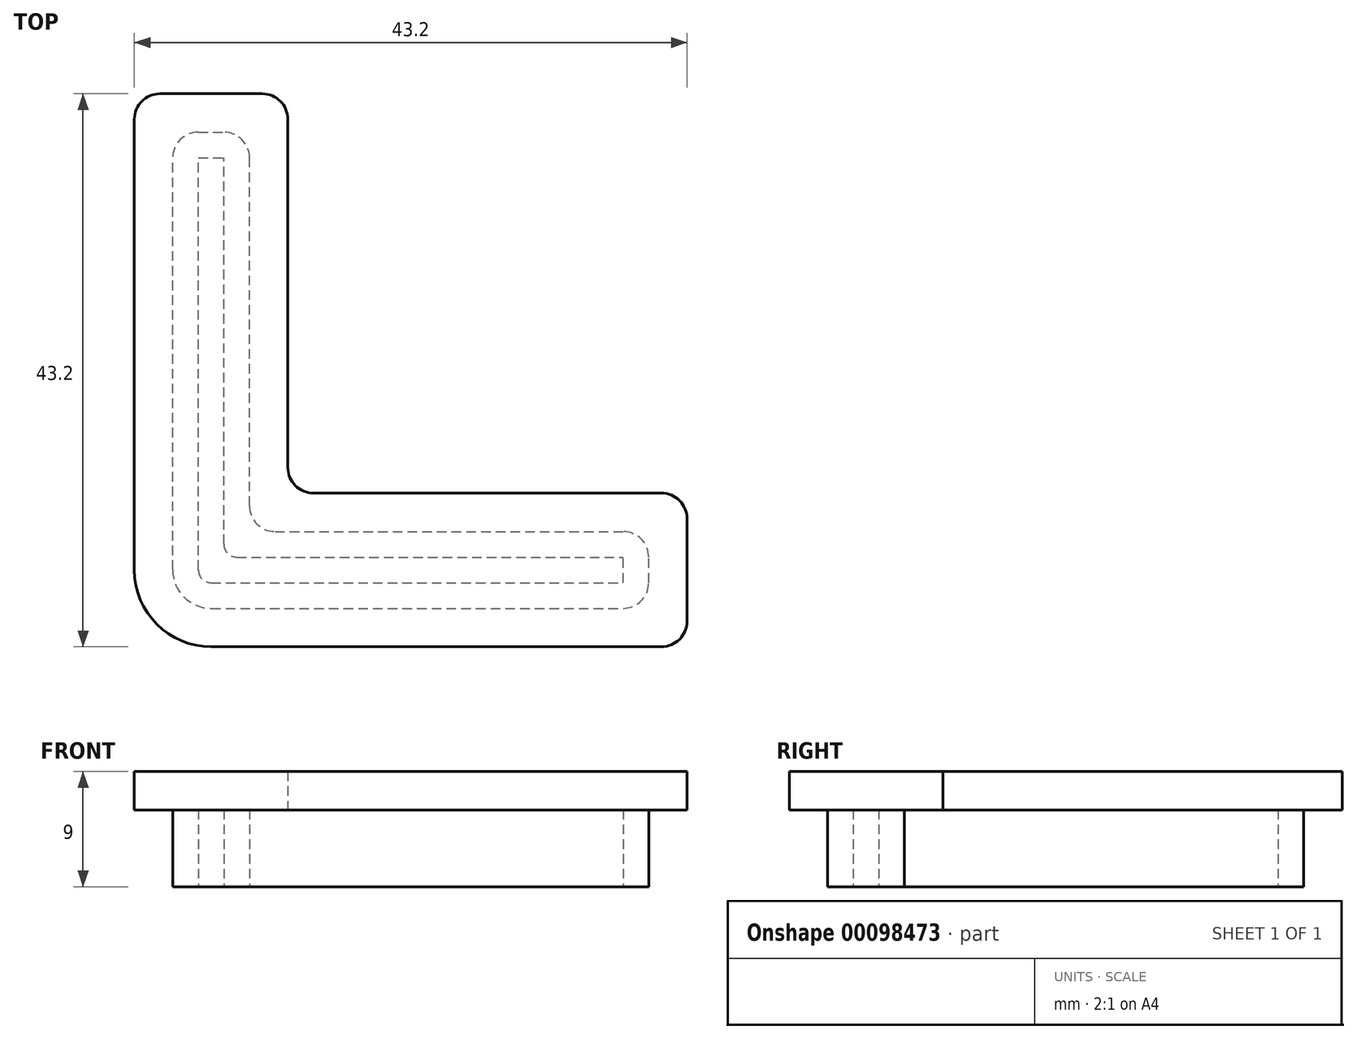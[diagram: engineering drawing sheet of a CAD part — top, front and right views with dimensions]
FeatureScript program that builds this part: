
annotation { "Feature Type Name" : "Feature", "Feature Type Description" : "" }
export const myFeature = defineFeature(function(context is Context, id is Id, definition is map)
    precondition{}
    {
        {
            var Q0;
            Q0=qCreatedBy(makeId("Top.planeOp"),FACE);
            var sketch = newSketch(context, id + "F0", { "sketchPlane" : qUnion([Q0])});
            skLineSegment(sketch, "E0", {"start": v(0, 0) * mm, "end": v(0, 32.2) * mm, "construction": true});
            skLineSegment(sketch, "E1", {"start": v(0, 0) * mm, "end": v(32.2, 0) * mm, "construction": true});
            skLineSegment(sketch, "E2.0", {"start": v(1, 2) * mm, "end": v(1, 32.2) * mm});
            skLineSegment(sketch, "E2.1", {"start": v(2, 1) * mm, "end": v(32.2, 1) * mm});
            skLineSegment(sketch, "E3.0", {"start": v(-1, 0) * mm, "end": v(-1, 32.2) * mm});
            skLineSegment(sketch, "E3.1", {"start": v(0, -1) * mm, "end": v(32.2, -1) * mm});
            skLineSegment(sketch, "E4", {"start": v(-1, 32.2) * mm, "end": v(1, 32.2) * mm});
            skLineSegment(sketch, "E5", {"start": v(32.2, -1) * mm, "end": v(32.2, 1) * mm});
            skPoint(sketch, "E6.visualSharp", {"position": v(1, 1) * mm});
            skArc(sketch, "E6.filletArc", {"start": v(1, 2) * mm, "mid": v(1.3, 1.3) * mm, "end": v(2, 1) * mm});
            skPoint(sketch, "E7.visualSharp", {"position": v(-1, -1) * mm});
            skArc(sketch, "E7.filletArc", {"start": v(-1, 0) * mm, "mid": v(-0.7, -0.7) * mm, "end": v(0, -1) * mm});
            skLineSegment(sketch, "E8.0", {"start": v(-3, 0) * mm, "end": v(-3, 34.2) * mm});
            skArc(sketch, "E8.1", {"start": v(-3, 0) * mm, "mid": v(-2.12, -2.12) * mm, "end": v(0, -3) * mm});
            skLineSegment(sketch, "E8.2", {"start": v(3, 5) * mm, "end": v(3, 34.2) * mm});
            skLineSegment(sketch, "E8.3", {"start": v(5, 3) * mm, "end": v(34.2, 3) * mm});
            skLineSegment(sketch, "E8.4", {"start": v(34.2, -3) * mm, "end": v(34.2, 3) * mm});
            skLineSegment(sketch, "E8.5", {"start": v(-3, 34.2) * mm, "end": v(3, 34.2) * mm});
            skLineSegment(sketch, "E8.6", {"start": v(0, -3) * mm, "end": v(34.2, -3) * mm});
            skPoint(sketch, "E9.visualSharp", {"position": v(3, 3) * mm});
            skArc(sketch, "E9.filletArc", {"start": v(3, 5) * mm, "mid": v(3.59, 3.59) * mm, "end": v(5, 3) * mm});
            skSolve(sketch);
        }
        {
            var Q0;
            Q0=makeQuery(id+"F0.imprint","IMPRINT",FACE,{"disambiguationData":[TD([[makeQuery(id+"F0.imprint","IMPRINT",EDGE,{"derivedFrom":sQuery(id+"F0.wireOp",EDGE,"E2.0")}),-1.0]])]});
            extrude(context, id + "F1", {"entities" : qUnion([Q0]), "depth" : 6 * mm});
        }
        {
            var Q0;
            Q0=makeQuery(id+"F1.opExtrude","CAP_FACE",FACE,{"disambiguationData":[OSD([sQuery(id+"F0.wireOp",EDGE,"E2.0"),sQuery(id+"F0.wireOp",EDGE,"E2.1"),sQuery(id+"F0.wireOp",EDGE,"E3.0"),sQuery(id+"F0.wireOp",EDGE,"E3.1"),sQuery(id+"F0.wireOp",EDGE,"E4"),sQuery(id+"F0.wireOp",EDGE,"E5"),sQuery(id+"F0.wireOp",EDGE,"E6.filletArc"),sQuery(id+"F0.wireOp",EDGE,"E7.filletArc"),sQuery(id+"F0.wireOp",EDGE,"E8.0"),sQuery(id+"F0.wireOp",EDGE,"E8.1"),sQuery(id+"F0.wireOp",EDGE,"E8.2"),sQuery(id+"F0.wireOp",EDGE,"E8.3"),sQuery(id+"F0.wireOp",EDGE,"E8.4"),sQuery(id+"F0.wireOp",EDGE,"E8.5"),sQuery(id+"F0.wireOp",EDGE,"E8.6"),sQuery(id+"F0.wireOp",EDGE,"E9.filletArc")])],"isStart":false});
            var sketch = newSketch(context, id + "F2", { "sketchPlane" : qUnion([Q0])});
            skLineSegment(sketch, "E10.0", {"start": v(-3, 34.2) * mm, "end": v(3, 34.2) * mm});
            skLineSegment(sketch, "E10.1", {"start": v(-3, 0) * mm, "end": v(-3, 34.2) * mm});
            skArc(sketch, "E10.2", {"start": v(-3, 0) * mm, "mid": v(-2.12, -2.12) * mm, "end": v(0, -3) * mm});
            skLineSegment(sketch, "E10.3", {"start": v(0, -3) * mm, "end": v(34.2, -3) * mm});
            skLineSegment(sketch, "E10.4", {"start": v(34.2, -3) * mm, "end": v(34.2, 3) * mm});
            skLineSegment(sketch, "E10.5", {"start": v(5, 3) * mm, "end": v(34.2, 3) * mm});
            skArc(sketch, "E10.6", {"start": v(3, 5) * mm, "mid": v(3.59, 3.59) * mm, "end": v(5, 3) * mm});
            skLineSegment(sketch, "E10.7", {"start": v(3, 5) * mm, "end": v(3, 34.2) * mm});
            skLineSegment(sketch, "E11.0", {"start": v(-6, 0) * mm, "end": v(-6, 37.2) * mm});
            skArc(sketch, "E11.1", {"start": v(-6, 0) * mm, "mid": v(-4.24, -4.24) * mm, "end": v(0, -6) * mm});
            skLineSegment(sketch, "E11.2", {"start": v(6, 6) * mm, "end": v(6, 37.2) * mm});
            skLineSegment(sketch, "E11.3", {"start": v(6, 6) * mm, "end": v(37.2, 6) * mm});
            skLineSegment(sketch, "E11.4", {"start": v(37.2, -6) * mm, "end": v(37.2, 6) * mm});
            skLineSegment(sketch, "E11.5", {"start": v(-6, 37.2) * mm, "end": v(6, 37.2) * mm});
            skLineSegment(sketch, "E11.6", {"start": v(0, -6) * mm, "end": v(37.2, -6) * mm});
            skSolve(sketch);
        }
        {
            var Q0;
            Q0 = qSketchRegion(id + "F2", true);
            var Q1;
            Q1=makeQuery(id+"F2.imprint","IMPRINT",FACE,{"disambiguationData":[TD([[makeQuery(id+"F2.imprint","IMPRINT",EDGE,{"derivedFrom":sQuery(id+"F2.wireOp",EDGE,"E10.0")}),-1.0]])]});
            var Q2;
            Q2=makeQuery(id+"F2.imprint","IMPRINT",FACE,{"disambiguationData":[TD([[makeQuery(id+"F2.imprint","IMPRINT",EDGE,{"derivedFrom":makeQuery(id+"F1.opExtrude","CAP_EDGE",EDGE,{"disambiguationData":[OSD([sQuery(id+"F0.wireOp",EDGE,"E2.0")])],"isStart":false})}),1.0]])]});
            extrude(context, id + "F3", {"entities" : qUnion([Q0, Q1, Q2]), "operationType" : NewBodyOperationType.ADD, "depth" : 3 * mm});
        }
        {
            var Q0;
            Q0=makeQuery(id+"F3.opExtrude","SWEPT_EDGE",EDGE,{"disambiguationData":[OSD([sQuery(id+"F2.wireOp",EDGE,"E11.2"),sQuery(id+"F2.wireOp",EDGE,"E11.5")])]});
            var Q1;
            Q1=makeQuery(id+"F3.opExtrude","SWEPT_EDGE",EDGE,{"disambiguationData":[OSD([sQuery(id+"F2.wireOp",EDGE,"E11.2"),sQuery(id+"F2.wireOp",EDGE,"E11.3")])]});
            var Q2;
            Q2=makeQuery(id+"F3.opExtrude","SWEPT_EDGE",EDGE,{"disambiguationData":[OSD([sQuery(id+"F2.wireOp",EDGE,"E11.3"),sQuery(id+"F2.wireOp",EDGE,"E11.4")])]});
            var Q3;
            Q3=makeQuery(id+"F3.opExtrude","SWEPT_EDGE",EDGE,{"disambiguationData":[OSD([sQuery(id+"F2.wireOp",EDGE,"E11.4"),sQuery(id+"F2.wireOp",EDGE,"E11.6")])]});
            var Q4;
            Q4=makeQuery(id+"F3.opExtrude","SWEPT_EDGE",EDGE,{"disambiguationData":[OSD([sQuery(id+"F2.wireOp",EDGE,"E11.0"),sQuery(id+"F2.wireOp",EDGE,"E11.5")])]});
            fillet(context, id + "F4", {"entities" : qUnion([Q0, Q1, Q2, Q3, Q4]), "radius" : 2 * mm, "tangentPropagation" : true, "allowEdgeOverflow" : false});
        }
        {
            var Q0;
            Q0=makeQuery(id+"F1.opExtrude","SWEPT_EDGE",EDGE,{"disambiguationData":[OSD([sQuery(id+"F0.wireOp",EDGE,"E8.0"),sQuery(id+"F0.wireOp",EDGE,"E8.5")])]});
            var Q1;
            Q1=makeQuery(id+"F1.opExtrude","SWEPT_EDGE",EDGE,{"disambiguationData":[OSD([sQuery(id+"F0.wireOp",EDGE,"E8.2"),sQuery(id+"F0.wireOp",EDGE,"E8.5")])]});
            var Q2;
            Q2=makeQuery(id+"F1.opExtrude","SWEPT_EDGE",EDGE,{"disambiguationData":[OSD([sQuery(id+"F0.wireOp",EDGE,"E8.3"),sQuery(id+"F0.wireOp",EDGE,"E8.4")])]});
            var Q3;
            Q3=makeQuery(id+"F1.opExtrude","SWEPT_EDGE",EDGE,{"disambiguationData":[OSD([sQuery(id+"F0.wireOp",EDGE,"E8.4"),sQuery(id+"F0.wireOp",EDGE,"E8.6")])]});
            fillet(context, id + "F5", {"entities" : qUnion([Q0, Q1, Q2, Q3]), "radius" : 2 * mm, "tangentPropagation" : true, "allowEdgeOverflow" : false});
        }
    });
